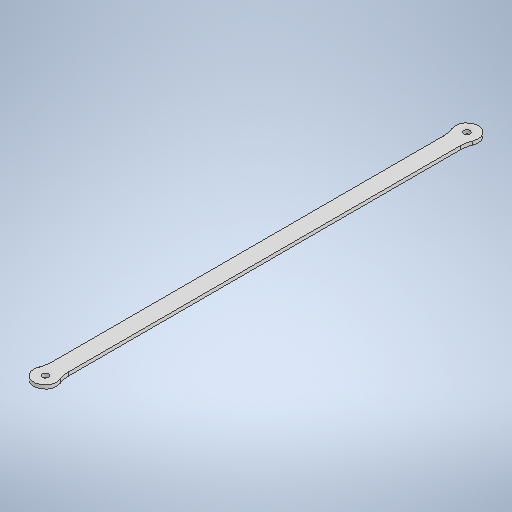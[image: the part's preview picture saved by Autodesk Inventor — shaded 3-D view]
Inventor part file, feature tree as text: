
AUTODESK INVENTOR PART (.ipt)
format: ipt  version: 2025.2 (Build 292293000, 293)  size: 282,624 bytes
history: native  units: in
note: dims shown in document units (in); Inventor stores cm internally (conversion verified against a paired STEP export)
features: extrude x2, sketch x2
ambient origin geometry x8: Origin, YZ Plane, XZ Plane, XY Plane, X Axis, Y Axis, Z Axis, Center Point
bodies: Solid1 (feature_tree)
feature tree (4):
  extrude  "Extrusion1"  Depth=0.1575in
  extrude  "Extrusion2"  TaperAngle=0.0deg  [1 undecoded]
  sketch  "Sketch1"  dims[d0=0.4291in d4=0.1575in]
  sketch  "Sketch2"  dims[d5=0.1575in d6=0.0in d7=0.4291in d8=7.874in d9=0.0in d10=0.2756in d12=0.1575in d13=0.2756in d14=0.0669in d15=0.0in d16=0.1181in d17=0.1181in d18=0.0669in d19=0.0in]
note: 1 required parameter value undecoded (feature->parameter linkage not recoverable at this tier; creation-order binding heuristic only, values carry confidence <= 0.55)
